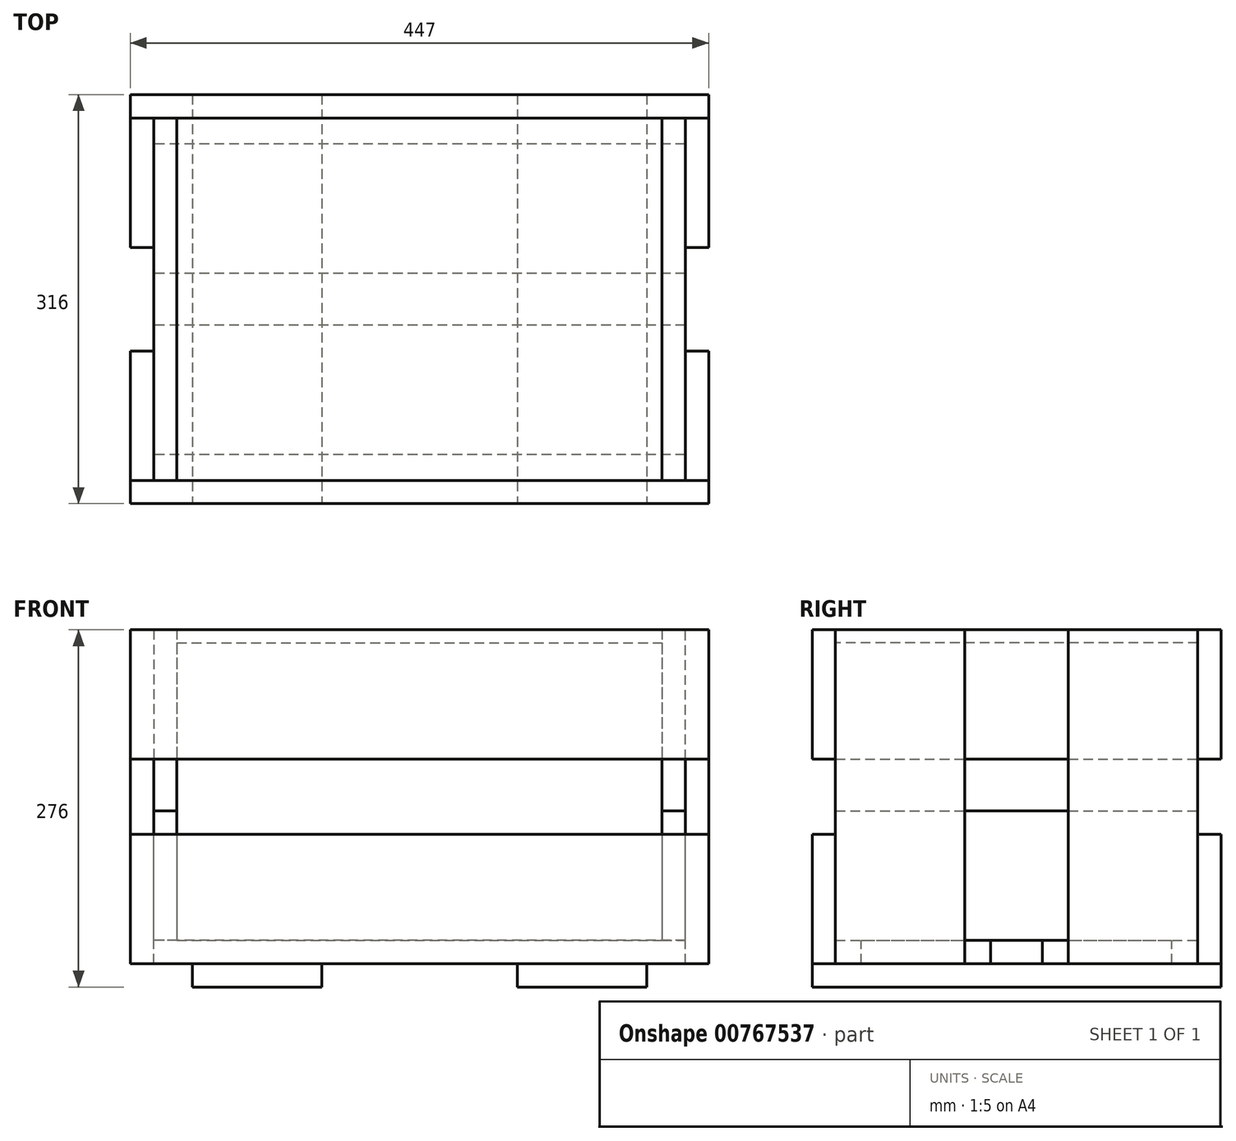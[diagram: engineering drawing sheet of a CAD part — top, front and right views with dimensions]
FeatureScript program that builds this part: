
annotation { "Feature Type Name" : "Feature", "Feature Type Description" : "" }
export const myFeature = defineFeature(function(context is Context, id is Id, definition is map)
    precondition{}
    {
        {
            var Q0;
            Q0=qCreatedBy(makeId("Top.planeOp"),FACE);
            var sketch = newSketch(context, id + "F0", { "sketchPlane" : qUnion([Q0])});
            skLineSegment(sketch, "E0.bottom", {"start": v(-187.5, 140) * mm, "end": v(187.5, 140) * mm});
            skLineSegment(sketch, "E0.top", {"start": v(-187.5, -140) * mm, "end": v(187.5, -140) * mm});
            skLineSegment(sketch, "E0.left", {"start": v(-187.5, 140) * mm, "end": v(-187.5, -140) * mm});
            skLineSegment(sketch, "E0.right", {"start": v(187.5, 140) * mm, "end": v(187.5, -140) * mm});
            skSolve(sketch);
        }
        {
            var Q0;
            Q0 = qSketchRegion(id + "F0", true);
            extrude(context, id + "F1", {"entities" : qUnion([Q0]), "depth" : 230 * mm, "offsetDistance" : 25 * mm});
        }
        {
            var Q0;
            Q0=makeQuery(id+"F1.opExtrude","SWEPT_FACE",FACE,{"disambiguationData":[OSD([sQuery(id+"F0.wireOp",EDGE,"E0.top")])]});
            var sketch = newSketch(context, id + "F2", { "sketchPlane" : qUnion([Q0])});
            skLineSegment(sketch, "E1.bottom", {"start": v(-223.5, 240) * mm, "end": v(223.5, 240) * mm});
            skLineSegment(sketch, "E1.top", {"start": v(-223.5, 140) * mm, "end": v(223.5, 140) * mm});
            skLineSegment(sketch, "E1.left", {"start": v(-223.5, 240) * mm, "end": v(-223.5, 140) * mm});
            skLineSegment(sketch, "E1.right", {"start": v(223.5, 240) * mm, "end": v(223.5, 140) * mm});
            skLineSegment(sketch, "E2", {"start": v(-276.18, 111) * mm, "end": v(291.6, 111) * mm, "construction": true});
            skLineSegment(sketch, "E3.MirrorCS", {"start": v(223.5, -18) * mm, "end": v(223.5, 82) * mm});
            skLineSegment(sketch, "E4.MirrorCS", {"start": v(-223.5, -18) * mm, "end": v(-223.5, 82) * mm});
            skLineSegment(sketch, "E5.MirrorCS", {"start": v(-223.5, 82) * mm, "end": v(223.5, 82) * mm});
            skLineSegment(sketch, "E6.MirrorCS", {"start": v(-223.5, -18) * mm, "end": v(223.5, -18) * mm});
            skSolve(sketch);
        }
        {
            var Q0;
            Q0 = qSketchRegion(id + "F2", true);
            extrude(context, id + "F3", {"entities" : qUnion([Q0]), "depth" : 18 * mm, "offsetDistance" : 25 * mm});
        }
        {
            var Q0;
            Q0=makeQuery(id+"F1.opExtrude","SWEPT_FACE",FACE,{"disambiguationData":[OSD([sQuery(id+"F0.wireOp",EDGE,"E0.bottom")])]});
            var sketch = newSketch(context, id + "F4", { "sketchPlane" : qUnion([Q0])});
            skLineSegment(sketch, "E7.bottom", {"start": v(187.5, 240) * mm, "end": v(205.5, 240) * mm});
            skLineSegment(sketch, "E7.top", {"start": v(187.5, 140) * mm, "end": v(205.5, 140) * mm});
            skLineSegment(sketch, "E7.left", {"start": v(187.5, 240) * mm, "end": v(187.5, 140) * mm});
            skLineSegment(sketch, "E7.right", {"start": v(205.5, 240) * mm, "end": v(205.5, 140) * mm});
            skLineSegment(sketch, "E8", {"start": v(147.4, 120) * mm, "end": v(241.33, 120) * mm, "construction": true});
            skLineSegment(sketch, "E9.MirrorCS", {"start": v(187.5, 0) * mm, "end": v(205.5, 0) * mm});
            skLineSegment(sketch, "E10.MirrorCS", {"start": v(187.5, 100) * mm, "end": v(205.5, 100) * mm});
            skLineSegment(sketch, "E11.MirrorCS", {"start": v(187.5, 0) * mm, "end": v(187.5, 100) * mm});
            skLineSegment(sketch, "E12.MirrorCS", {"start": v(205.5, 0) * mm, "end": v(205.5, 100) * mm});
            skLineSegment(sketch, "E13", {"start": v(0, 261.2) * mm, "end": v(0, -48.04) * mm, "construction": true});
            skLineSegment(sketch, "E14.MirrorCS", {"start": v(-187.5, 240) * mm, "end": v(-205.5, 240) * mm});
            skLineSegment(sketch, "E15.MirrorCS", {"start": v(-187.5, 140) * mm, "end": v(-205.5, 140) * mm});
            skLineSegment(sketch, "E16.MirrorCS", {"start": v(-187.5, 240) * mm, "end": v(-187.5, 140) * mm});
            skLineSegment(sketch, "E17.MirrorCS", {"start": v(-205.5, 240) * mm, "end": v(-205.5, 140) * mm});
            skLineSegment(sketch, "E18.MirrorCS", {"start": v(-187.5, 100) * mm, "end": v(-205.5, 100) * mm});
            skLineSegment(sketch, "E19.MirrorCS", {"start": v(-187.5, 0) * mm, "end": v(-187.5, 100) * mm});
            skLineSegment(sketch, "E20.MirrorCS", {"start": v(-205.5, 0) * mm, "end": v(-205.5, 100) * mm});
            skLineSegment(sketch, "E21.MirrorCS", {"start": v(-187.5, 0) * mm, "end": v(-205.5, 0) * mm});
            skLineSegment(sketch, "E22.bottom", {"start": v(-167.5, -18) * mm, "end": v(-67.5, -18) * mm});
            skLineSegment(sketch, "E22.top", {"start": v(-167.5, -36) * mm, "end": v(-67.5, -36) * mm});
            skLineSegment(sketch, "E22.left", {"start": v(-167.5, -18) * mm, "end": v(-167.5, -36) * mm});
            skLineSegment(sketch, "E22.right", {"start": v(-67.5, -18) * mm, "end": v(-67.5, -36) * mm});
            skLineSegment(sketch, "E23.MirrorCS", {"start": v(167.5, -18) * mm, "end": v(167.5, -36) * mm});
            skLineSegment(sketch, "E24.MirrorCS", {"start": v(167.5, -18) * mm, "end": v(67.5, -18) * mm});
            skLineSegment(sketch, "E25.MirrorCS", {"start": v(167.5, -36) * mm, "end": v(67.5, -36) * mm});
            skLineSegment(sketch, "E26.MirrorCS", {"start": v(67.5, -18) * mm, "end": v(67.5, -36) * mm});
            skSolve(sketch);
        }
        {
            var Q0;
            {var subQ4=sQuery(id+"F4.wireOp",EDGE,"E14.MirrorCS");Q0=makeQuery(id+"F4.imprint","IMPRINT",FACE,{"disambiguationData":[TD([[makeQuery(id+"F4.imprint","IMPRINT",EDGE,{"derivedFrom":subQ4}),1.0]])]});}
            var Q1;
            Q1=makeQuery(id+"F4.imprint","IMPRINT",FACE,{"disambiguationData":[TD([[makeQuery(id+"F4.imprint","IMPRINT",EDGE,{"derivedFrom":sQuery(id+"F4.wireOp",EDGE,"E18.MirrorCS")}),1.0]])]});
            var Q2;
            {var subQ4=sQuery(id+"F4.wireOp",EDGE,"E7.bottom");Q2=makeQuery(id+"F4.imprint","IMPRINT",FACE,{"disambiguationData":[TD([[makeQuery(id+"F4.imprint","IMPRINT",EDGE,{"derivedFrom":subQ4}),-1.0]])]});}
            var Q3;
            Q3=makeQuery(id+"F4.imprint","IMPRINT",FACE,{"disambiguationData":[TD([[makeQuery(id+"F4.imprint","IMPRINT",EDGE,{"derivedFrom":sQuery(id+"F4.wireOp",EDGE,"E9.MirrorCS")}),1.0]])]});
            var Q4;
            Q4=makeQuery(id+"F3.opExtrude","CAP_FACE",FACE,{"disambiguationData":[OSD([sQuery(id+"F2.wireOp",EDGE,"E3.MirrorCS"),sQuery(id+"F2.wireOp",EDGE,"E4.MirrorCS"),sQuery(id+"F2.wireOp",EDGE,"E5.MirrorCS"),sQuery(id+"F2.wireOp",EDGE,"E6.MirrorCS")])],"isStart":true});
            extrude(context, id + "F5", {"entities" : qUnion([Q0, Q1, Q2, Q3]), "endBound" : BoundingType.UP_TO_SURFACE, "oppositeDirection" : true, "depth" : 25 * mm, "endBoundEntityFace" : qUnion([Q4]), "offsetDistance" : 25 * mm});
        }
        {
            var Q0;
            Q0=makeQuery(id+"F1.opExtrude","SWEPT_FACE",FACE,{"disambiguationData":[OSD([sQuery(id+"F0.wireOp",EDGE,"E0.right")])]});
            var sketch = newSketch(context, id + "F6", { "sketchPlane" : qUnion([Q0])});
            skLineSegment(sketch, "E27.bottom", {"start": v(140, 240) * mm, "end": v(158, 240) * mm});
            skLineSegment(sketch, "E27.top", {"start": v(140, 140) * mm, "end": v(158, 140) * mm});
            skLineSegment(sketch, "E27.left", {"start": v(140, 240) * mm, "end": v(140, 140) * mm});
            skLineSegment(sketch, "E27.right", {"start": v(158, 240) * mm, "end": v(158, 140) * mm});
            skLineSegment(sketch, "E28", {"start": v(98.53, 111) * mm, "end": v(304.93, 111) * mm, "construction": true});
            skLineSegment(sketch, "E29.MirrorCS", {"start": v(140, -18) * mm, "end": v(158, -18) * mm});
            skLineSegment(sketch, "E30.MirrorCS", {"start": v(140, -18) * mm, "end": v(140, 82) * mm});
            skLineSegment(sketch, "E31.MirrorCS", {"start": v(158, -18) * mm, "end": v(158, 82) * mm});
            skLineSegment(sketch, "E32.MirrorCS", {"start": v(140, 82) * mm, "end": v(158, 82) * mm});
            skLineSegment(sketch, "E33.bottom", {"start": v(-120, 0) * mm, "end": v(-20, 0) * mm});
            skLineSegment(sketch, "E33.top", {"start": v(-120, -18) * mm, "end": v(-20, -18) * mm});
            skLineSegment(sketch, "E33.left", {"start": v(-120, 0) * mm, "end": v(-120, -18) * mm});
            skLineSegment(sketch, "E33.right", {"start": v(-20, 0) * mm, "end": v(-20, -18) * mm});
            skLineSegment(sketch, "E34", {"start": v(0, -30.8) * mm, "end": v(0, -127.76) * mm, "construction": true});
            skLineSegment(sketch, "E35.MirrorCS", {"start": v(120, 0) * mm, "end": v(120, -18) * mm});
            skLineSegment(sketch, "E36.MirrorCS", {"start": v(20, 0) * mm, "end": v(20, -18) * mm});
            skLineSegment(sketch, "E37.MirrorCS", {"start": v(120, -18) * mm, "end": v(20, -18) * mm});
            skLineSegment(sketch, "E38.MirrorCS", {"start": v(120, 0) * mm, "end": v(20, 0) * mm});
            skSolve(sketch);
        }
        {
            var Q0;
            {var subQ4=sQuery(id+"F6.wireOp",EDGE,"E27.bottom");Q0=makeQuery(id+"F6.imprint","IMPRINT",FACE,{"disambiguationData":[TD([[makeQuery(id+"F6.imprint","IMPRINT",EDGE,{"derivedFrom":subQ4}),-1.0]])]});}
            var Q1;
            {var subQ4=sQuery(id+"F6.wireOp",EDGE,"E29.MirrorCS");Q1=makeQuery(id+"F6.imprint","IMPRINT",FACE,{"disambiguationData":[TD([[makeQuery(id+"F6.imprint","IMPRINT",EDGE,{"derivedFrom":subQ4}),1.0]])]});}
            var Q2;
            Q2=makeQuery(id+"F3.opExtrude","SWEPT_FACE",FACE,{"disambiguationData":[OSD([sQuery(id+"F2.wireOp",EDGE,"E3.MirrorCS")])]});
            var Q3;
            Q3=makeQuery(id+"F3.opExtrude","SWEPT_FACE",FACE,{"disambiguationData":[OSD([sQuery(id+"F2.wireOp",EDGE,"E1.left")])]});
            extrude(context, id + "F7", {"entities" : qUnion([Q0, Q1]), "endBound" : BoundingType.UP_TO_SURFACE, "depth" : 25 * mm, "endBoundEntityFace" : qUnion([Q2]), "offsetDistance" : 25 * mm, "hasSecondDirection" : true, "secondDirectionBound" : SecondDirectionBoundingType.UP_TO_SURFACE, "secondDirectionOppositeDirection" : true, "secondDirectionDepth" : 25 * mm, "secondDirectionBoundEntityFace" : qUnion([Q3])});
        }
        {
            var Q0;
            Q0=makeQuery(id+"F3.opExtrude","SWEPT_FACE",FACE,{"disambiguationData":[OSD([sQuery(id+"F2.wireOp",EDGE,"E1.bottom")])]});
            var sketch = newSketch(context, id + "F8", { "sketchPlane" : qUnion([Q0])});
            skLineSegment(sketch, "E39.bottom", {"start": v(-223.5, -140) * mm, "end": v(-205.5, -140) * mm});
            skLineSegment(sketch, "E39.top", {"start": v(-223.5, -40) * mm, "end": v(-205.5, -40) * mm});
            skLineSegment(sketch, "E39.left", {"start": v(-223.5, -140) * mm, "end": v(-223.5, -40) * mm});
            skLineSegment(sketch, "E39.right", {"start": v(-205.5, -140) * mm, "end": v(-205.5, -40) * mm});
            skLineSegment(sketch, "E40", {"start": v(-246.43, 0) * mm, "end": v(0, 0) * mm, "construction": true});
            skLineSegment(sketch, "E41", {"start": v(0, 0) * mm, "end": v(0, -206.3) * mm, "construction": true});
            skLineSegment(sketch, "E42.MirrorCS", {"start": v(-223.5, 140) * mm, "end": v(-223.5, 40) * mm});
            skLineSegment(sketch, "E43.MirrorCS", {"start": v(-205.5, 140) * mm, "end": v(-205.5, 40) * mm});
            skLineSegment(sketch, "E44.MirrorCS", {"start": v(-223.5, 40) * mm, "end": v(-205.5, 40) * mm});
            skLineSegment(sketch, "E45.MirrorCS", {"start": v(-223.5, 140) * mm, "end": v(-205.5, 140) * mm});
            skLineSegment(sketch, "E46.MirrorCS", {"start": v(223.5, -40) * mm, "end": v(205.5, -40) * mm});
            skLineSegment(sketch, "E47.MirrorCS", {"start": v(223.5, -140) * mm, "end": v(205.5, -140) * mm});
            skLineSegment(sketch, "E48.MirrorCS", {"start": v(223.5, 40) * mm, "end": v(205.5, 40) * mm});
            skLineSegment(sketch, "E49.MirrorCS", {"start": v(223.5, -140) * mm, "end": v(223.5, -40) * mm});
            skLineSegment(sketch, "E50.MirrorCS", {"start": v(223.5, 140) * mm, "end": v(205.5, 140) * mm});
            skLineSegment(sketch, "E51.MirrorCS", {"start": v(205.5, 140) * mm, "end": v(205.5, 40) * mm});
            skLineSegment(sketch, "E52.MirrorCS", {"start": v(223.5, 140) * mm, "end": v(223.5, 40) * mm});
            skLineSegment(sketch, "E53.MirrorCS", {"start": v(205.5, -140) * mm, "end": v(205.5, -40) * mm});
            skSolve(sketch);
        }
        {
            var Q0;
            Q0 = qSketchRegion(id + "F8", true);
            var Q1;
            Q1=makeQuery(id+"F7.opExtrude","SWEPT_FACE",FACE,{"disambiguationData":[OSD([sQuery(id+"F6.wireOp",EDGE,"E29.MirrorCS")])]});
            extrude(context, id + "F9", {"entities" : qUnion([Q0]), "endBound" : BoundingType.UP_TO_SURFACE, "oppositeDirection" : true, "depth" : 25 * mm, "endBoundEntityFace" : qUnion([Q1]), "offsetDistance" : 25 * mm});
        }
        {
            var Q0;
            Q0=makeQuery(id+"F6.imprint","IMPRINT",FACE,{"disambiguationData":[TD([[makeQuery(id+"F6.imprint","IMPRINT",EDGE,{"derivedFrom":sQuery(id+"F6.wireOp",EDGE,"E33.bottom")}),1.0]])]});
            var Q1;
            Q1=makeQuery(id+"F6.imprint","IMPRINT",FACE,{"disambiguationData":[TD([[makeQuery(id+"F6.imprint","IMPRINT",EDGE,{"derivedFrom":sQuery(id+"F6.wireOp",EDGE,"E35.MirrorCS")}),-1.0]])]});
            var Q2;
            Q2=makeQuery(id+"F5.opExtrude","SWEPT_FACE",FACE,{"disambiguationData":[OSD([sQuery(id+"F4.wireOp",EDGE,"E20.MirrorCS")])]});
            var Q3;
            Q3=makeQuery(id+"F5.opExtrude","SWEPT_FACE",FACE,{"disambiguationData":[OSD([sQuery(id+"F4.wireOp",EDGE,"E12.MirrorCS")])]});
            extrude(context, id + "F10", {"entities" : qUnion([Q0, Q1]), "endBound" : BoundingType.UP_TO_SURFACE, "depth" : 25 * mm, "endBoundEntityFace" : qUnion([Q2]), "offsetDistance" : 25 * mm, "hasSecondDirection" : true, "secondDirectionBound" : SecondDirectionBoundingType.UP_TO_SURFACE, "secondDirectionOppositeDirection" : true, "secondDirectionDepth" : 25 * mm, "secondDirectionBoundEntityFace" : qUnion([Q3])});
        }
        {
            var Q0;
            Q0=makeQuery(id+"F3.opExtrude","CAP_FACE",FACE,{"disambiguationData":[OSD([sQuery(id+"F2.wireOp",EDGE,"E3.MirrorCS"),sQuery(id+"F2.wireOp",EDGE,"E4.MirrorCS"),sQuery(id+"F2.wireOp",EDGE,"E5.MirrorCS"),sQuery(id+"F2.wireOp",EDGE,"E6.MirrorCS")])],"isStart":false});
            var sketch = newSketch(context, id + "F11", { "sketchPlane" : qUnion([Q0])});
            skLineSegment(sketch, "E54.bottom", {"start": v(-175.5, -36) * mm, "end": v(-75.5, -36) * mm});
            skLineSegment(sketch, "E54.top", {"start": v(-175.5, -18) * mm, "end": v(-75.5, -18) * mm});
            skLineSegment(sketch, "E54.left", {"start": v(-175.5, -36) * mm, "end": v(-175.5, -18) * mm});
            skLineSegment(sketch, "E54.right", {"start": v(-75.5, -36) * mm, "end": v(-75.5, -18) * mm});
            skLineSegment(sketch, "E55", {"start": v(0, -95.62) * mm, "end": v(0, 24.11) * mm, "construction": true});
            skLineSegment(sketch, "E56.MirrorCS", {"start": v(75.5, -36) * mm, "end": v(75.5, -18) * mm});
            skLineSegment(sketch, "E57.MirrorCS", {"start": v(175.5, -36) * mm, "end": v(175.5, -18) * mm});
            skLineSegment(sketch, "E58.MirrorCS", {"start": v(175.5, -18) * mm, "end": v(75.5, -18) * mm});
            skLineSegment(sketch, "E59.MirrorCS", {"start": v(175.5, -36) * mm, "end": v(75.5, -36) * mm});
            skSolve(sketch);
        }
        {
            var Q0;
            Q0 = qSketchRegion(id + "F11", true);
            var Q1;
            Q1=makeQuery(id+"F7.opExtrude","SWEPT_FACE",FACE,{"disambiguationData":[OSD([sQuery(id+"F6.wireOp",EDGE,"E31.MirrorCS")])]});
            extrude(context, id + "F12", {"entities" : qUnion([Q0]), "endBound" : BoundingType.UP_TO_SURFACE, "oppositeDirection" : true, "depth" : 25 * mm, "endBoundEntityFace" : qUnion([Q1]), "offsetDistance" : 25 * mm});
        }
    });
